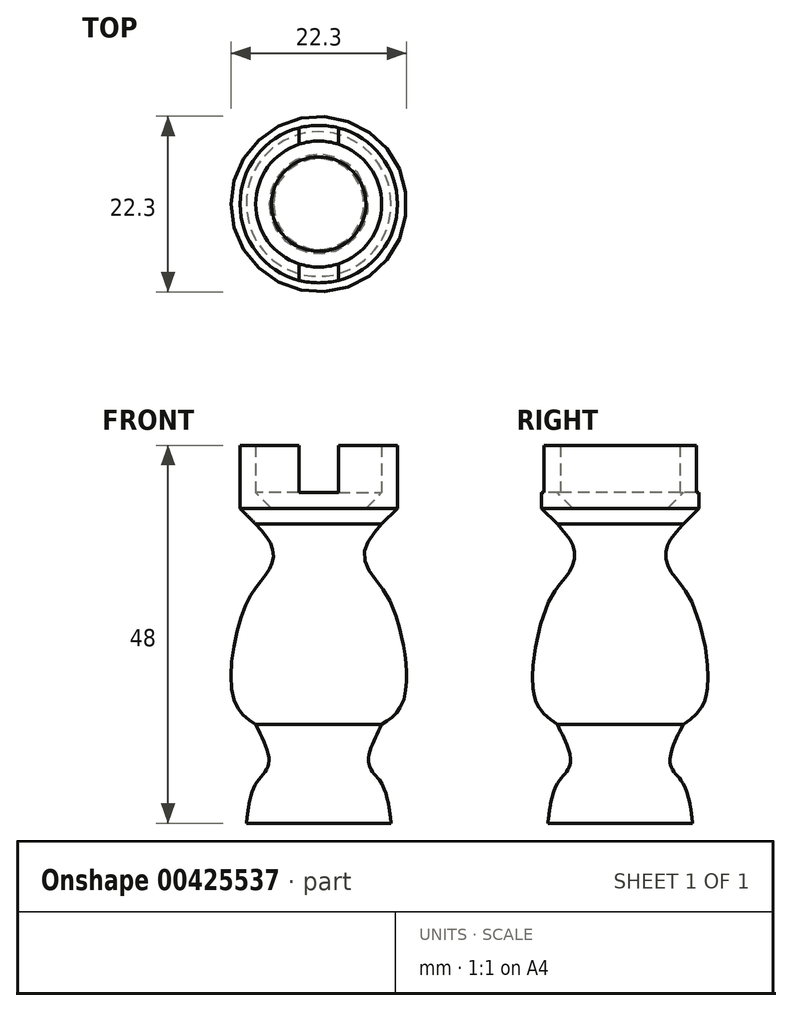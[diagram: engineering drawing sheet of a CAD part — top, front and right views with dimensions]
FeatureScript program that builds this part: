
annotation { "Feature Type Name" : "Feature", "Feature Type Description" : "" }
export const myFeature = defineFeature(function(context is Context, id is Id, definition is map)
    precondition{}
    {
        {
            var Q0;
            Q0=qCreatedBy(makeId("Front.planeOp"),FACE);
            var sketch = newSketch(context, id + "F0", { "sketchPlane" : qUnion([Q0])});
            skLineSegment(sketch, "E0.bottom", {"start": v(0, 0) * mm, "end": v(12.5, 0) * mm});
            skLineSegment(sketch, "E0.top", {"start": v(0, 48) * mm, "end": v(12.5, 48) * mm});
            skLineSegment(sketch, "E0.left", {"start": v(0, 0) * mm, "end": v(0, 48) * mm});
            skLineSegment(sketch, "E0.right", {"start": v(12.5, 0) * mm, "end": v(12.5, 48) * mm});
            skLineSegment(sketch, "E1.bottom", {"start": v(0, 48) * mm, "end": v(8, 48) * mm});
            skLineSegment(sketch, "E1.top", {"start": v(0, 40) * mm, "end": v(8, 40) * mm});
            skLineSegment(sketch, "E1.left", {"start": v(0, 48) * mm, "end": v(0, 40) * mm});
            skLineSegment(sketch, "E1.right", {"start": v(8, 48) * mm, "end": v(8, 40) * mm});
            skLineSegment(sketch, "E2", {"start": v(10, 48) * mm, "end": v(10, 40) * mm});
            skLineSegment(sketch, "E3", {"start": v(8, 38) * mm, "end": v(0, 38) * mm});
            skLineSegment(sketch, "E4", {"start": v(10, 40) * mm, "end": v(8, 38) * mm});
            skPoint(sketch, "E5.orphan", {"position": v(10, 38) * mm});
            skLineSegment(sketch, "E6", {"start": v(0, 2.5) * mm, "end": v(12.5, 2.5) * mm});
            skFitSpline(sketch, "E7", {"points": [v(8, 38) * mm, v(5.85, 34.78) * mm, v(6.4, 32.02) * mm, v(9.1, 28.08) * mm, v(10.87, 15.96) * mm, v(8, 12.53) * mm], "startDerivative": vector(-16.43, -18.44) * mm, "endDerivative": vector(-19.32, -12.88) * mm});
            skFitSpline(sketch, "E8", {"points": [v(8, 12.53) * mm, v(6.36, 7.55) * mm, v(8, 5) * mm, v(9.2, 0) * mm], "startDerivative": vector(-7.8, -15.35) * mm, "endDerivative": vector(1.86, -15.57) * mm});
            skSolve(sketch);
        }
        {
            var Q0;
            {var subQ0=sQuery(id+"F0.wireOp",EDGE,"E1.top");Q0=makeQuery(id+"F0.imprint","IMPRINT",FACE,{"disambiguationData":[TD([[makeQuery(id+"F0.imprint","IMPRINT",EDGE,{"derivedFrom":subQ0}),-1.0]])]});}
            var Q1;
            {var subQ6=sQuery(id+"F0.wireOp",EDGE,"E3");Q1=makeQuery(id+"F0.imprint","IMPRINT",FACE,{"disambiguationData":[TD([[makeQuery(id+"F0.imprint","IMPRINT",EDGE,{"derivedFrom":subQ6}),1.0]])]});}
            var Q2;
            {var subQ0=sQuery(id+"F0.wireOp",EDGE,"E0.left");var subQ1=sQuery(id+"F0.wireOp",EDGE,"E0.bottom");var subQ2=makeQuery(id+"F0.imprint","INTERSECT",VERTEX,{"derivedFrom":[subQ1,subQ0]});Q2=makeQuery(id+"F0.imprint","IMPRINT",FACE,{"disambiguationData":[TD([[makeQuery(id+"F0.imprint","IMPRINT",EDGE,{"disambiguationData":[TD([[subQ2,-1.0]])],"derivedFrom":subQ1}),1.0]])]});}
            var Q3;
            Q3=sQuery(id+"F0.wireOp",EDGE,"E0.left");
            revolve(context, id + "F1", {"entities" : qUnion([Q0, Q1, Q2]), "axis" : qUnion([Q3]), "revolveType" : RevolveType.FULL});
        }
        {
            var Q0;
            Q0=makeQuery(id+"F1.opRevolve","SWEPT_FACE",FACE,{"disambiguationData":[OSD([sQuery(id+"F0.wireOp",EDGE,"E0.top")])]});
            var sketch = newSketch(context, id + "F2", { "sketchPlane" : qUnion([Q0])});
            skLineSegment(sketch, "E9.bottom", {"start": v(-2.5, 15) * mm, "end": v(2.5, 15) * mm});
            skLineSegment(sketch, "E9.top", {"start": v(-2.5, -15) * mm, "end": v(2.5, -15) * mm});
            skLineSegment(sketch, "E9.left", {"start": v(-2.5, 15) * mm, "end": v(-2.5, -15) * mm});
            skLineSegment(sketch, "E9.right", {"start": v(2.5, 15) * mm, "end": v(2.5, -15) * mm});
            skPoint(sketch, "E9.middle", {"position": v(0, 0) * mm});
            skSolve(sketch);
        }
        {
            var Q0;
            Q0 = qSketchRegion(id + "F2", true);
            extrude(context, id + "F3", {"entities" : qUnion([Q0]), "operationType" : NewBodyOperationType.REMOVE, "oppositeDirection" : true, "depth" : 6 * mm});
        }
        {
            var Q0;
            Q0=makeQuery(id+"F1.opRevolve","SWEPT_FACE",FACE,{"disambiguationData":[OSD([sQuery(id+"F0.wireOp",EDGE,"E1.top")])]});
            chamfer(context, id + "F4", {"entities" : qUnion([Q0]), "width" : 2 * mm, "tangentPropagation" : true});
        }
    });
